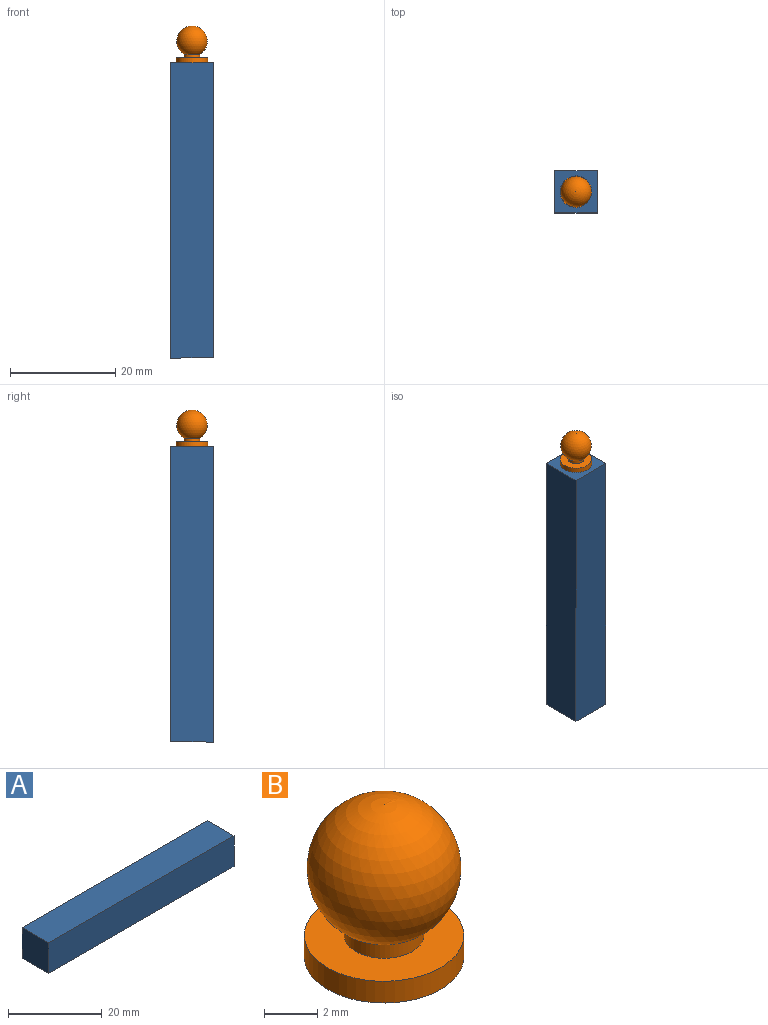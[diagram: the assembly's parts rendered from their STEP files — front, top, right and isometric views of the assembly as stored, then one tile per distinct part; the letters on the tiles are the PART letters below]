
ASSEMBLY  parts=2 mates=1
PART A: 6 faces, bbox 56x8x8 mm
  f0: plane 56x8mm, normal (0,0,-1), area 448mm2, adj f1,f3,f4,f5
  f1: plane 8x8mm, normal (1,0,0), area 64mm2, adj f0,f2,f4,f5
  f2: plane 56x8mm, normal (0,0,1), area 448mm2, adj f1,f3,f4,f5
  f3: plane 8x8mm, normal (-1,0,0), area 64mm2, adj f0,f2,f4,f5
  f4: plane 56x8mm, normal (0,-1,0), area 448mm2, adj f0,f1,f2,f3
  f5: plane 56x8mm, normal (0,1,0), area 448mm2, adj f0,f1,f2,f3
PART B: 5 faces, bbox 6x6x7 mm
  f0: plane 6x6mm, normal (0,0,-1), area 28.3mm2, adj f4
  f1: sphere r=2.9mm, area 98.1mm2, adj f2
  f2: cylinder r=1.5mm len=3mm, axis (0,0,1), area 5.8mm2, adj f1,f3
  f3: plane 6x6mm, normal (0,0,1), area 21.2mm2, adj f2,f4
  f4: cylinder r=3mm len=6mm, axis (0,0,1), area 18.8mm2, adj f0,f3
PLACE A rot(axis=(0.71,0,0.71),180deg) t=(-4.16,-0.25,-3.73)mm
PLACE B t=(-0.16,-0.25,24.27)mm
MATE fastened B.f2 <-> A.f1  axis (0,0,-1) through (-0.16,-0.25,24.27)mm
